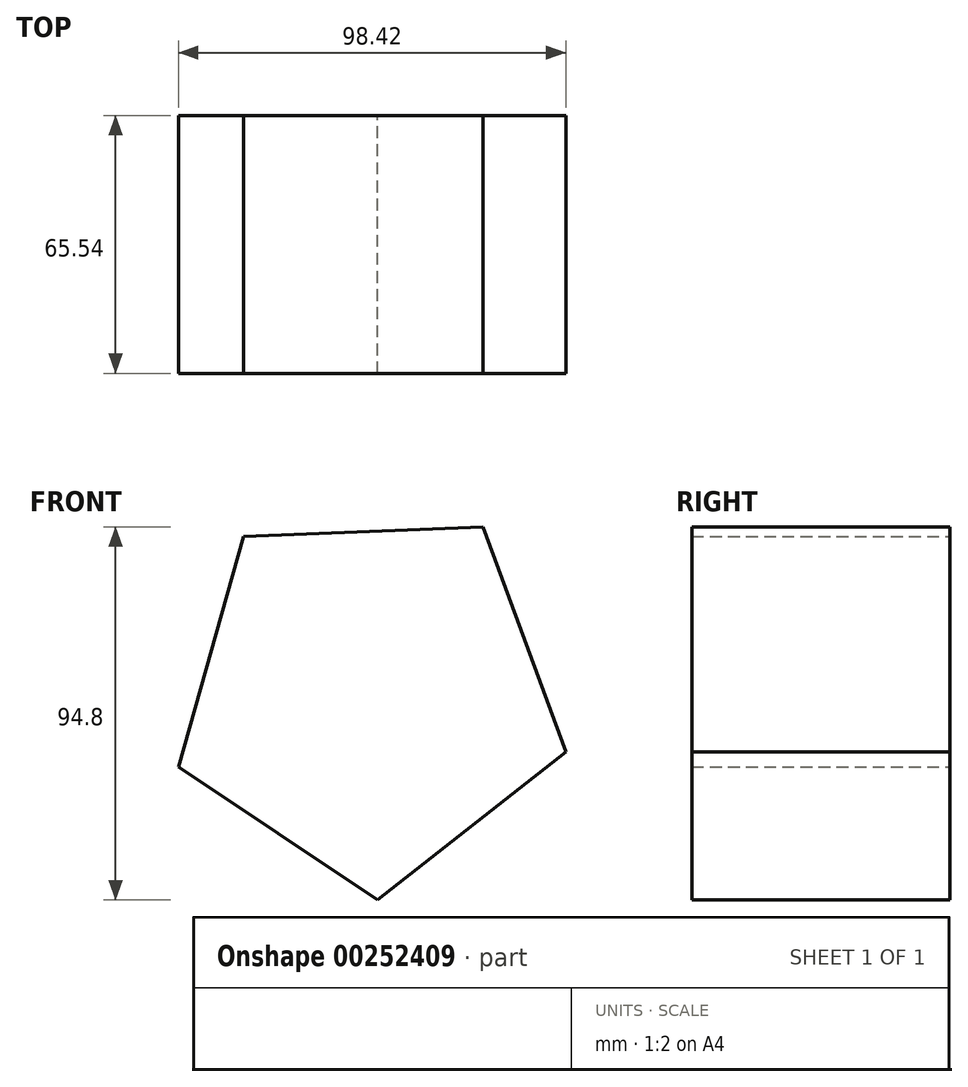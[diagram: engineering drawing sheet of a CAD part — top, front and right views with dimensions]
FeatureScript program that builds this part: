
annotation { "Feature Type Name" : "Feature", "Feature Type Description" : "" }
export const myFeature = defineFeature(function(context is Context, id is Id, definition is map)
    precondition{}
    {
        {
            var Q0;
            Q0=qCreatedBy(makeId("Front.planeOp"),FACE);
            var sketch = newSketch(context, id + "F0", { "sketchPlane" : qUnion([Q0])});
            skCircle(sketch, "E0.cCircle", {"center": v(0, 0) * mm, "radius": 51.78 * mm, "construction": true});
            skLineSegment(sketch, "E0.0", {"start": v(-32.06, 40.66) * mm, "end": v(28.76, 43.06) * mm});
            skLineSegment(sketch, "E0.1", {"start": v(28.76, 43.06) * mm, "end": v(49.84, -14.05) * mm});
            skLineSegment(sketch, "E0.2", {"start": v(49.84, -14.05) * mm, "end": v(2.04, -51.74) * mm});
            skLineSegment(sketch, "E0.3", {"start": v(2.04, -51.74) * mm, "end": v(-48.58, -17.93) * mm});
            skLineSegment(sketch, "E0.4", {"start": v(-48.58, -17.93) * mm, "end": v(-32.06, 40.66) * mm});
            skSolve(sketch);
        }
        {
            var Q0;
            Q0=makeQuery(id+"F0.imprint","IMPRINT",FACE,{"disambiguationData":[TD([[makeQuery(id+"F0.imprint","IMPRINT",EDGE,{"derivedFrom":sQuery(id+"F0.wireOp",EDGE,"E0.0")}),-1.0]])]});
            extrude(context, id + "F1", {"entities" : qUnion([Q0]), "endBound" : BoundingType.SYMMETRIC, "depth" : 65.53 * mm});
        }
    });
